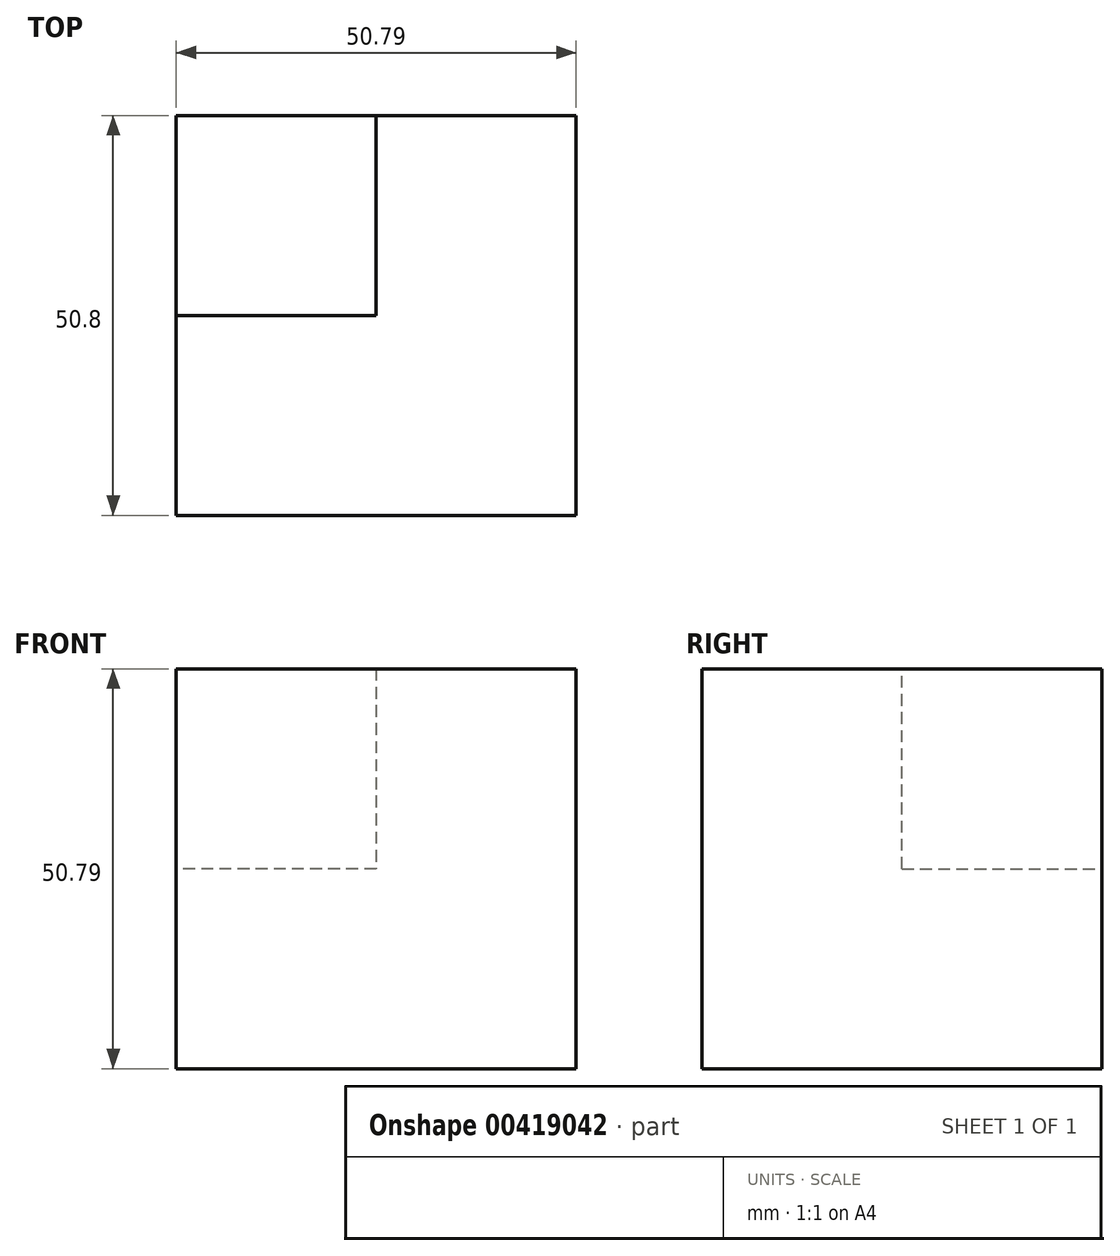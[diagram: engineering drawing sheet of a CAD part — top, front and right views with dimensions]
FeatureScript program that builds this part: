
annotation { "Feature Type Name" : "Feature", "Feature Type Description" : "" }
export const myFeature = defineFeature(function(context is Context, id is Id, definition is map)
    precondition{}
    {
        {
            var Q0;
            Q0=qCreatedBy(makeId("Front.planeOp"),FACE);
            var sketch = newSketch(context, id + "F0", { "sketchPlane" : qUnion([Q0])});
            skLineSegment(sketch, "E0", {"start": v(0, 0) * mm, "end": v(-50.8, 0) * mm});
            skLineSegment(sketch, "E1", {"start": v(-50.8, 0) * mm, "end": v(-50.8, 50.8) * mm});
            skLineSegment(sketch, "E2", {"start": v(-50.8, 50.8) * mm, "end": v(0, 50.8) * mm});
            skLineSegment(sketch, "E3", {"start": v(0, 50.8) * mm, "end": v(0, 0) * mm});
            skLineSegment(sketch, "E4", {"start": v(-25.4, 50.8) * mm, "end": v(-25.4, 25.4) * mm});
            skLineSegment(sketch, "E5", {"start": v(-25.4, 25.4) * mm, "end": v(-50.8, 25.4) * mm});
            skSolve(sketch);
        }
        {
            var Q0;
            Q0 = qSketchRegion(id + "F0", true);
            extrude(context, id + "F1", {"entities" : qUnion([Q0]), "depth" : 50.8 * mm});
        }
        {
            var Q0;
            {var subQ4=sQuery(id+"F0.wireOp",EDGE,"E4");Q0=makeQuery(id+"F0.imprint","IMPRINT",FACE,{"disambiguationData":[TD([[makeQuery(id+"F0.imprint","IMPRINT",EDGE,{"derivedFrom":subQ4}),-1.0]])]});}
            extrude(context, id + "F2", {"entities" : qUnion([Q0]), "operationType" : NewBodyOperationType.REMOVE, "depth" : 25.4 * mm});
        }
    });
